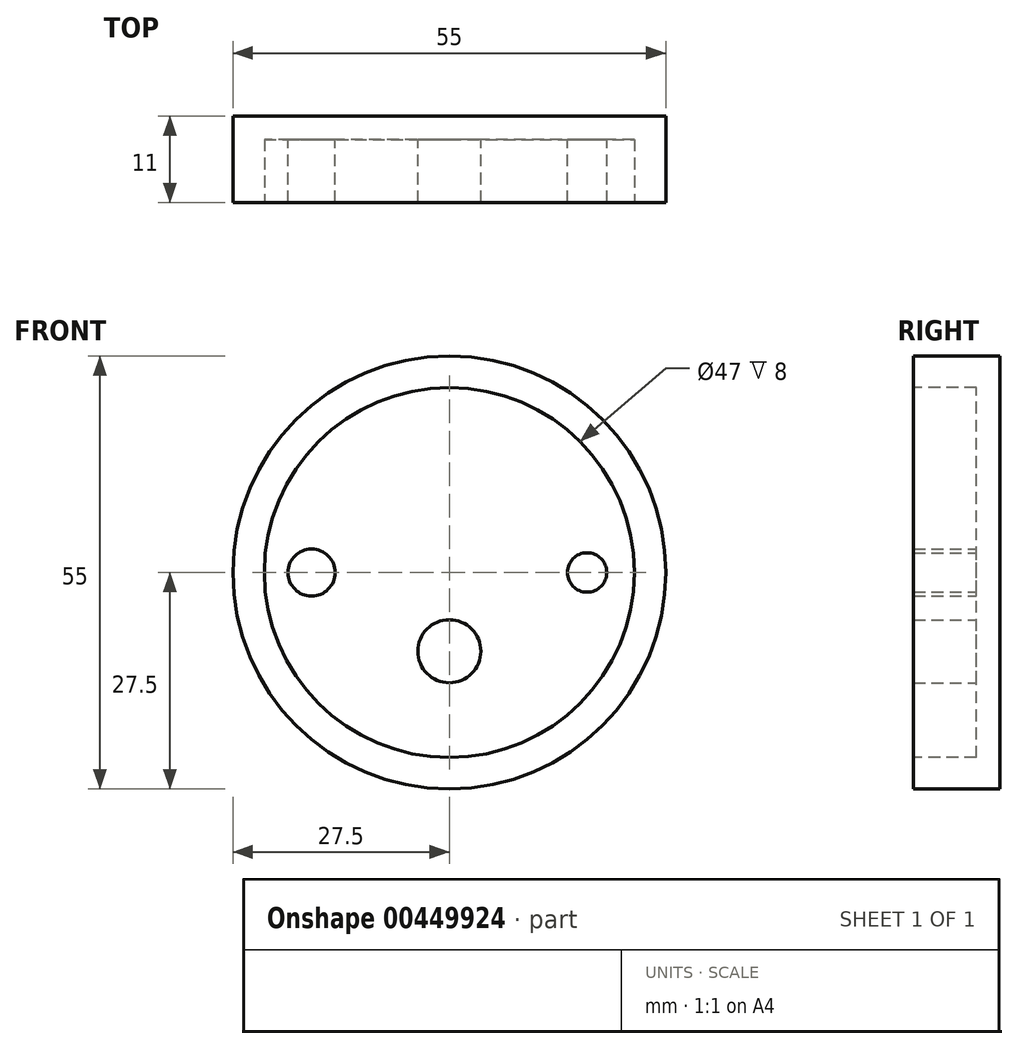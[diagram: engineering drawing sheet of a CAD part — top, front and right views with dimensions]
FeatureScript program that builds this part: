
annotation { "Feature Type Name" : "Feature", "Feature Type Description" : "" }
export const myFeature = defineFeature(function(context is Context, id is Id, definition is map)
    precondition{}
    {
        {
            var Q0;
            Q0=qCreatedBy(makeId("Front.planeOp"),FACE);
            var sketch = newSketch(context, id + "F0", { "sketchPlane" : qUnion([Q0])});
            skCircle(sketch, "E0", {"center": v(0, 0) * mm, "radius": 27.5 * mm});
            skSolve(sketch);
        }
        {
            var Q0;
            Q0 = qSketchRegion(id + "F0", true);
            extrude(context, id + "F1", {"entities" : qUnion([Q0]), "depth" : 11 * mm});
        }
        {
            var Q0;
            Q0=makeQuery(id+"F1.opExtrude","CAP_FACE",FACE,{"disambiguationData":[OSD([sQuery(id+"F0.wireOp",EDGE,"E0")])],"isStart":false});
            var sketch = newSketch(context, id + "F2", { "sketchPlane" : qUnion([Q0])});
            skCircle(sketch, "E1", {"center": v(0, 0) * mm, "radius": 23.5 * mm});
            skSolve(sketch);
        }
        {
            var Q0;
            Q0 = qSketchRegion(id + "F2", true);
            extrude(context, id + "F3", {"entities" : qUnion([Q0]), "operationType" : NewBodyOperationType.REMOVE, "oppositeDirection" : true, "depth" : 8 * mm});
        }
        {
            var Q0;
            Q0=makeQuery(id+"F3.boolean.opBoolean","COPY",FACE,{"derivedFrom":makeQuery(id+"F3.opExtrude","CAP_FACE",FACE,{"disambiguationData":[OSD([sQuery(id+"F2.wireOp",EDGE,"E1")])],"isStart":false})});
            var sketch = newSketch(context, id + "F4", { "sketchPlane" : qUnion([Q0])});
            skCircle(sketch, "E2", {"center": v(0, -10) * mm, "radius": 4 * mm});
            skCircle(sketch, "E3", {"center": v(-17.5, 0) * mm, "radius": 3 * mm});
            skCircle(sketch, "E4", {"center": v(17.5, 0) * mm, "radius": 2.5 * mm});
            skSolve(sketch);
        }
        {
            var Q0;
            Q0 = qSketchRegion(id + "F4", true);
            extrude(context, id + "F5", {"entities" : qUnion([Q0]), "operationType" : NewBodyOperationType.ADD, "depth" : 8 * mm});
        }
    });
